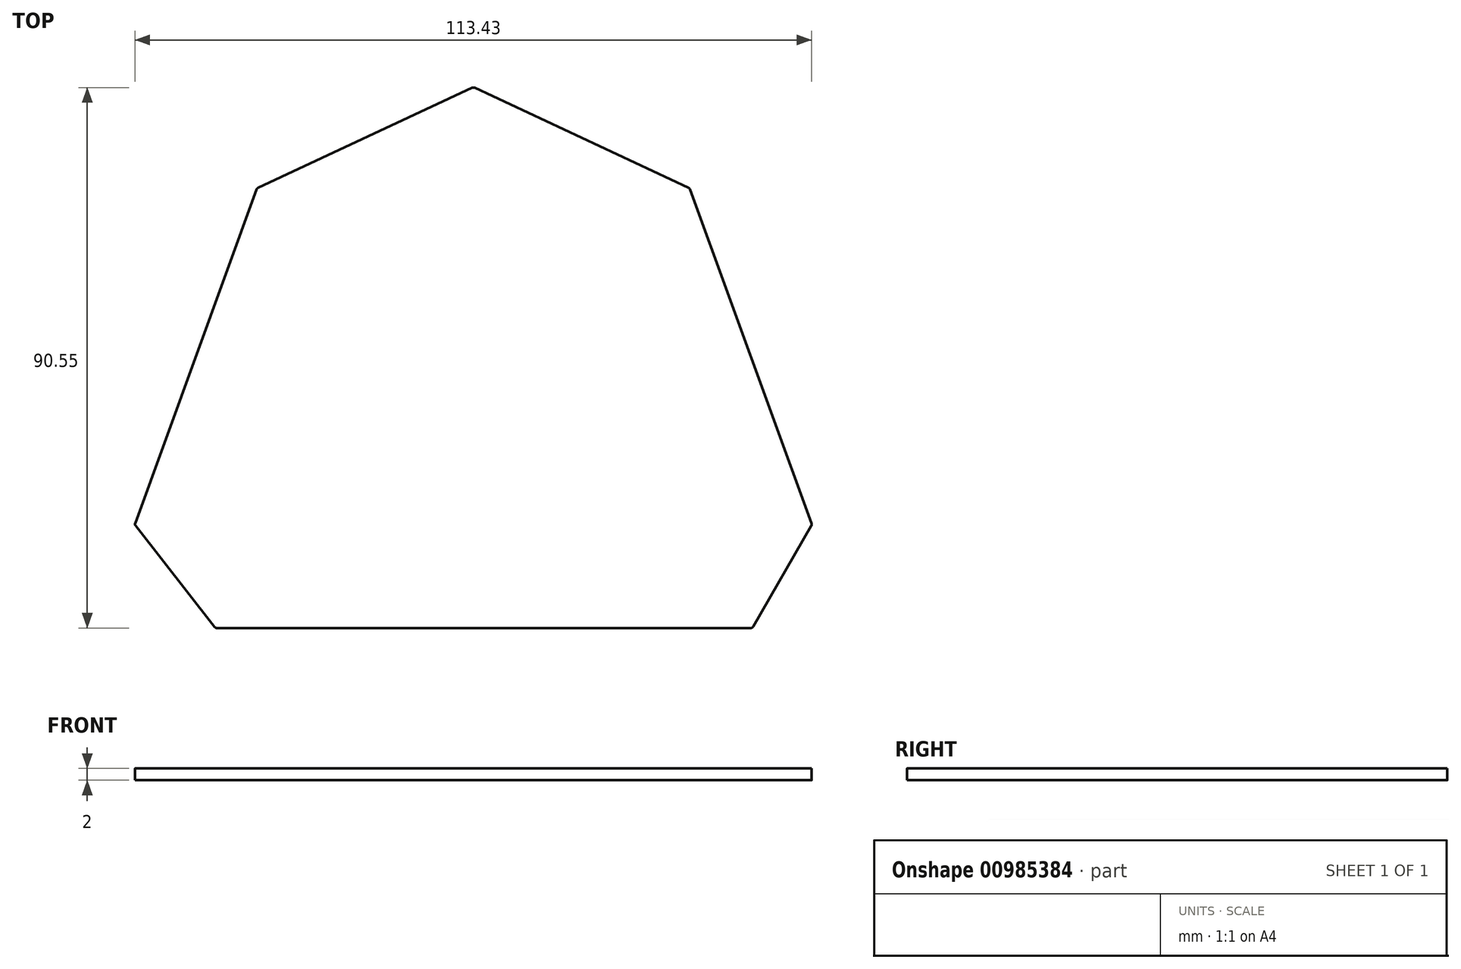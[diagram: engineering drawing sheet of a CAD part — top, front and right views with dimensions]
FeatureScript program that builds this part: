
annotation { "Feature Type Name" : "Feature", "Feature Type Description" : "" }
export const myFeature = defineFeature(function(context is Context, id is Id, definition is map)
    precondition{}
    {
        {
            var Q0;
            Q0=qCreatedBy(makeId("Top.planeOp"),FACE);
            var sketch = newSketch(context, id + "F0", { "sketchPlane" : qUnion([Q0])});
            skLineSegment(sketch, "E0", {"start": v(-34.12, -17.32) * mm, "end": v(55.88, -17.32) * mm});
            skLineSegment(sketch, "E1", {"start": v(55.88, -17.32) * mm, "end": v(65.88, 0) * mm});
            skLineSegment(sketch, "E2", {"start": v(65.88, 0) * mm, "end": v(45.36, 56.38) * mm});
            skLineSegment(sketch, "E3", {"start": v(45.36, 56.38) * mm, "end": v(9.1, 73.29) * mm});
            skLineSegment(sketch, "E4", {"start": v(9.1, 73.29) * mm, "end": v(-27.14, 56.38) * mm});
            skLineSegment(sketch, "E5", {"start": v(-27.14, 56.38) * mm, "end": v(-47.66, 0) * mm});
            skLineSegment(sketch, "E6", {"start": v(-47.66, 0) * mm, "end": v(-34.12, -17.32) * mm});
            skSolve(sketch);
        }
        {
            var Q0;
            Q0 = qSketchRegion(id + "F0", true);
            extrude(context, id + "F1", {"entities" : qUnion([Q0]), "depth" : 2 * mm, "offsetDistance" : 25 * mm});
        }
        {
            var Q0;
            Q0=makeQuery(id+"F1.opExtrude","SWEPT_EDGE",EDGE,{"disambiguationData":[OSD([sQuery(id+"F0.wireOp",EDGE,"E3"),sQuery(id+"F0.wireOp",EDGE,"E4")])]});
            var Q1;
            Q1=makeQuery(id+"F1.opExtrude","SWEPT_EDGE",EDGE,{"disambiguationData":[OSD([sQuery(id+"F0.wireOp",EDGE,"E4"),sQuery(id+"F0.wireOp",EDGE,"E5")])]});
            var Q2;
            Q2=makeQuery(id+"F1.opExtrude","SWEPT_EDGE",EDGE,{"disambiguationData":[OSD([sQuery(id+"F0.wireOp",EDGE,"E5"),sQuery(id+"F0.wireOp",EDGE,"E6")])]});
            var Q3;
            Q3=makeQuery(id+"F1.opExtrude","SWEPT_EDGE",EDGE,{"disambiguationData":[OSD([sQuery(id+"F0.wireOp",EDGE,"E0"),sQuery(id+"F0.wireOp",EDGE,"E6")])]});
            var Q4;
            Q4=makeQuery(id+"F1.opExtrude","SWEPT_EDGE",EDGE,{"disambiguationData":[OSD([sQuery(id+"F0.wireOp",EDGE,"E0"),sQuery(id+"F0.wireOp",EDGE,"E1")])]});
            var Q5;
            Q5=makeQuery(id+"F1.opExtrude","SWEPT_EDGE",EDGE,{"disambiguationData":[OSD([sQuery(id+"F0.wireOp",EDGE,"E1"),sQuery(id+"F0.wireOp",EDGE,"E2")])]});
            var Q6;
            Q6=makeQuery(id+"F1.opExtrude","SWEPT_EDGE",EDGE,{"disambiguationData":[OSD([sQuery(id+"F0.wireOp",EDGE,"E2"),sQuery(id+"F0.wireOp",EDGE,"E3")])]});
            fillet(context, id + "F2", {"entities" : qUnion([Q0, Q1, Q2, Q3, Q4, Q5, Q6]), "radius" : 0.5 * mm, "tangentPropagation" : true, "allowEdgeOverflow" : false});
        }
    });
